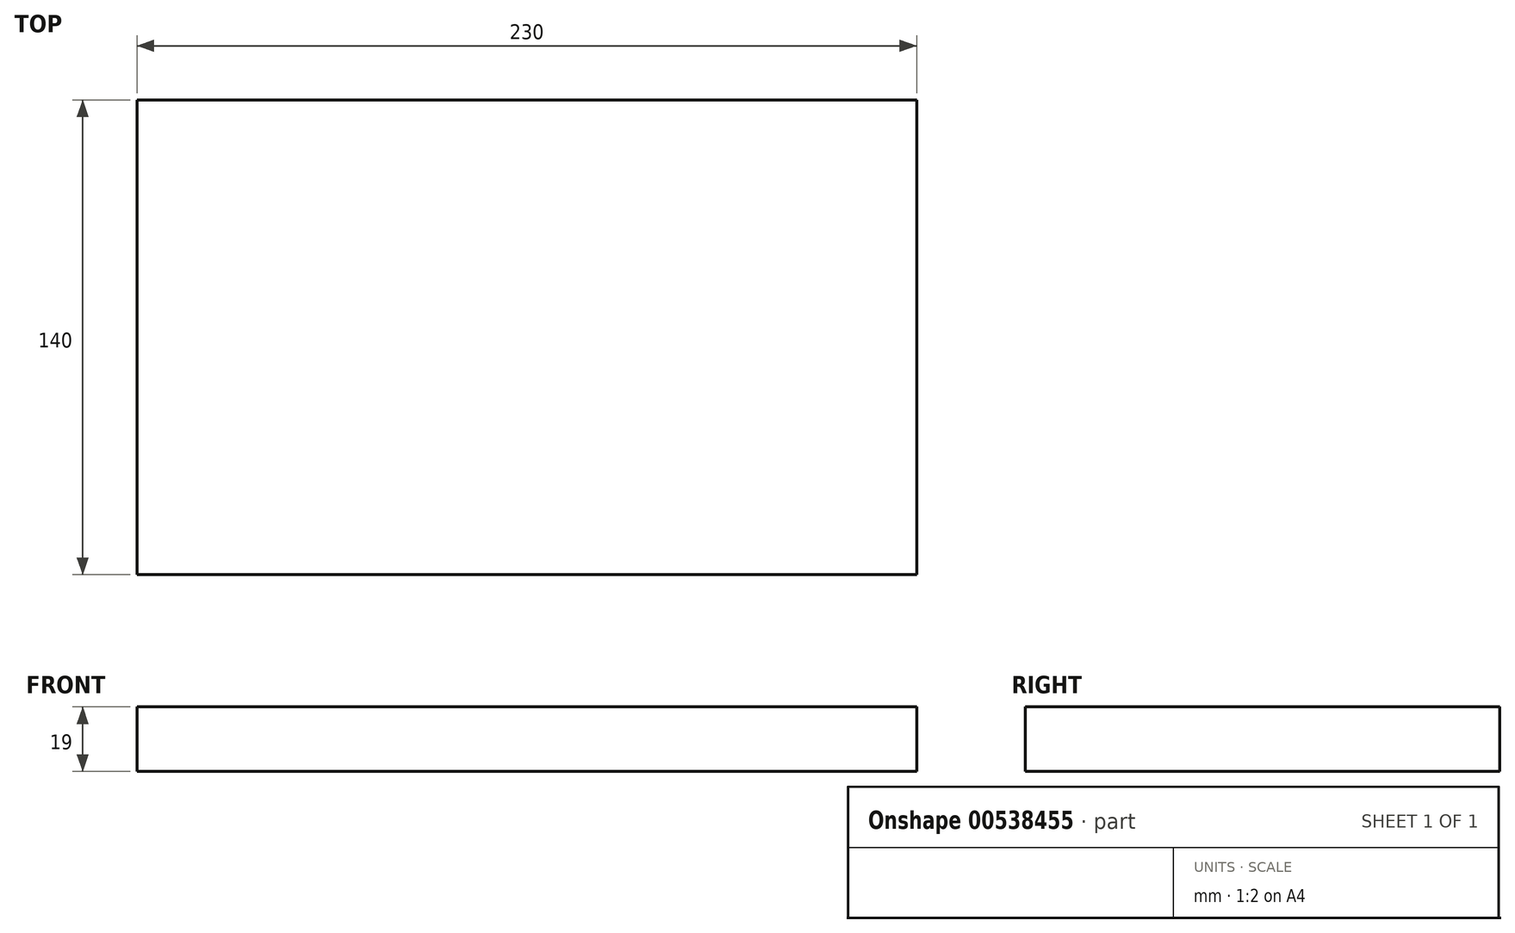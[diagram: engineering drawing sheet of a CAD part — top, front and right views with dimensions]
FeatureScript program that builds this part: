
annotation { "Feature Type Name" : "Feature", "Feature Type Description" : "" }
export const myFeature = defineFeature(function(context is Context, id is Id, definition is map)
    precondition{}
    {
        {
            var Q0;
            Q0=qCreatedBy(makeId("Top.planeOp"),FACE);
            var sketch = newSketch(context, id + "F0", { "sketchPlane" : qUnion([Q0])});
            skLineSegment(sketch, "E0.bottom", {"start": v(115, -70) * mm, "end": v(-115, -70) * mm});
            skLineSegment(sketch, "E0.top", {"start": v(115, 70) * mm, "end": v(-115, 70) * mm});
            skLineSegment(sketch, "E0.left", {"start": v(115, -70) * mm, "end": v(115, 70) * mm});
            skLineSegment(sketch, "E0.right", {"start": v(-115, -70) * mm, "end": v(-115, 70) * mm});
            skPoint(sketch, "E0.middle", {"position": v(0, 0) * mm});
            skSolve(sketch);
        }
        {
            var Q0;
            Q0 = qSketchRegion(id + "F0", true);
            extrude(context, id + "F1", {"entities" : qUnion([Q0]), "depth" : 19 * mm, "offsetDistance" : 25 * mm});
        }
    });
